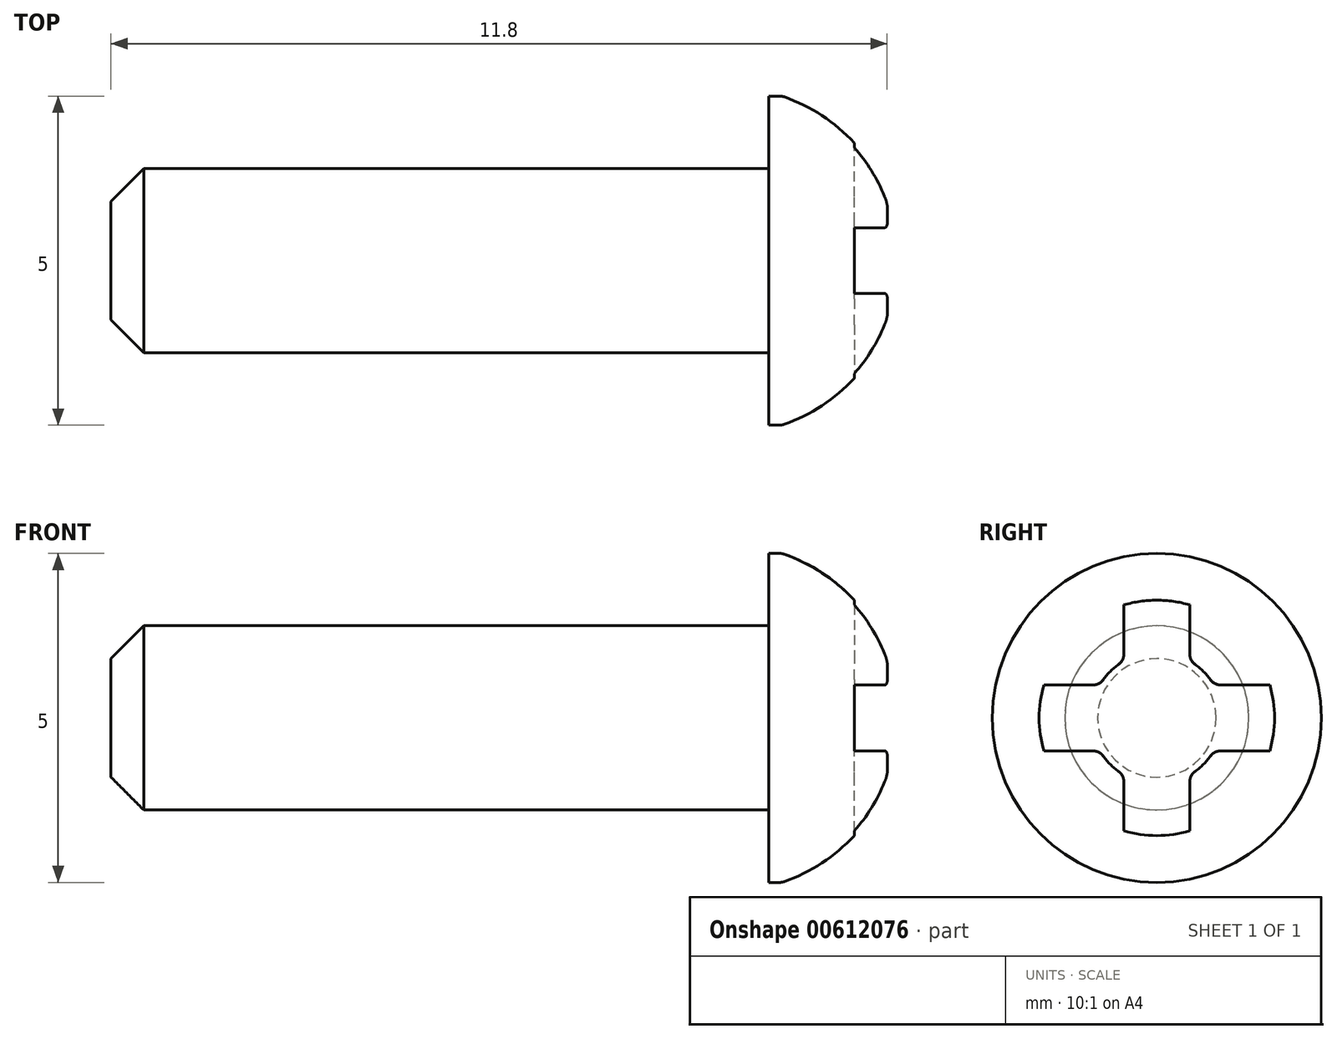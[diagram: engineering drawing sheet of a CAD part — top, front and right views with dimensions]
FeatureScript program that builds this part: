
annotation { "Feature Type Name" : "Feature", "Feature Type Description" : "" }
export const myFeature = defineFeature(function(context is Context, id is Id, definition is map)
    precondition{}
    {
        {
            var Q0;
            Q0=qCreatedBy(makeId("Front.planeOp"),FACE);
            var sketch = newSketch(context, id + "F0", { "sketchPlane" : qUnion([Q0])});
            skLineSegment(sketch, "E0", {"start": v(0, 1.4) * mm, "end": v(0, 2.5) * mm});
            skLineSegment(sketch, "E1", {"start": v(0, 1.4) * mm, "end": v(-10, 1.4) * mm});
            skLineSegment(sketch, "E2", {"start": v(-10, 1.4) * mm, "end": v(-10, 0) * mm});
            skLineSegment(sketch, "E3", {"start": v(-10, 0) * mm, "end": v(2, 0) * mm});
            skLineSegment(sketch, "E4", {"start": v(0, 0) * mm, "end": v(32.43, 0) * mm, "construction": true});
            skLineSegment(sketch, "E5", {"start": v(0, 2.5) * mm, "end": v(0.2, 2.5) * mm});
            skArc(sketch, "E6", {"start": v(2, 0) * mm, "mid": v(1.5, 1.54) * mm, "end": v(0.2, 2.5) * mm});
            skLineSegment(sketch, "E7", {"start": v(2, 0) * mm, "end": v(2, 6.78) * mm, "construction": true});
            skSolve(sketch);
        }
        {
            var Q0;
            Q0=makeQuery(id+"F0.imprint","IMPRINT",FACE,{"disambiguationData":[TD([[makeQuery(id+"F0.imprint","IMPRINT",EDGE,{"derivedFrom":sQuery(id+"F0.wireOp",EDGE,"E0")}),-1.0]])]});
            var Q1;
            Q1=sQuery(id+"F0.wireOp",EDGE,"E4");
            revolve(context, id + "F1", {"entities" : qUnion([Q0]), "axis" : qUnion([Q1]), "revolveType" : RevolveType.FULL});
        }
        {
            var Q0;
            Q0=makeQuery(id+"F1.opRevolve","SWEPT_EDGE",EDGE,{"disambiguationData":[OSD([sQuery(id+"F0.wireOp",EDGE,"E1"),sQuery(id+"F0.wireOp",EDGE,"E2")])]});
            chamfer(context, id + "F2", {"entities" : qUnion([Q0]), "width" : .5 * mm, "tangentPropagation" : true});
        }
        {
            var Q0;
            Q0=qCreatedBy(makeId("Right.planeOp"),FACE);
            cPlane(context, id + "F3", {"entities" : qUnion([Q0]), "cplaneType" : CPlaneType.OFFSET, "offset" : 3 * mm, "width" : 150 * mm, "height" : 150 * mm});
        }
        {
            var Q0;
            Q0=qCreatedBy(id+"F3.planeOp",FACE);
            var sketch = newSketch(context, id + "F4", { "sketchPlane" : qUnion([Q0])});
            skLineSegment(sketch, "E8.bottom", {"start": v(0, 0) * mm, "end": v(3, 0) * mm, "construction": true});
            skLineSegment(sketch, "E8.top", {"start": v(0, 3) * mm, "end": v(0.5, 3) * mm});
            skLineSegment(sketch, "E8.left", {"start": v(0, 0) * mm, "end": v(0, 3) * mm, "construction": true});
            skLineSegment(sketch, "E8.right", {"start": v(3, 0) * mm, "end": v(3, 0.5) * mm});
            skLineSegment(sketch, "E9", {"start": v(0.5, 3) * mm, "end": v(0.5, 0.87) * mm});
            skLineSegment(sketch, "E10", {"start": v(0.87, 0.5) * mm, "end": v(3, 0.5) * mm});
            skArc(sketch, "E11", {"start": v(0.87, 0.5) * mm, "mid": v(0.7, 0.7) * mm, "end": v(0.5, 0.87) * mm});
            skLineSegment(sketch, "E12.0.MirrorCS", {"start": v(0, -3) * mm, "end": v(0.5, -3) * mm});
            skLineSegment(sketch, "E13.0.MirrorCS", {"start": v(0.5, -3) * mm, "end": v(0.5, -0.87) * mm});
            skArc(sketch, "E14.0.MirrorCS", {"start": v(0.87, -0.5) * mm, "mid": v(0.7, -0.7) * mm, "end": v(0.5, -0.87) * mm});
            skLineSegment(sketch, "E15.0.MirrorCS", {"start": v(0.87, -0.5) * mm, "end": v(3, -0.5) * mm});
            skLineSegment(sketch, "E16.0.MirrorCS", {"start": v(3, 0) * mm, "end": v(3, -0.5) * mm});
            skLineSegment(sketch, "E17.0.MirrorCS", {"start": v(0, 3) * mm, "end": v(-0.5, 3) * mm});
            skLineSegment(sketch, "E18.0.MirrorCS", {"start": v(-0.5, 3) * mm, "end": v(-0.5, 0.87) * mm});
            skArc(sketch, "E19.0.MirrorCS", {"start": v(-0.87, 0.5) * mm, "mid": v(-0.7, 0.7) * mm, "end": v(-0.5, 0.87) * mm});
            skLineSegment(sketch, "E20.0.MirrorCS", {"start": v(-0.87, 0.5) * mm, "end": v(-3, 0.5) * mm});
            skLineSegment(sketch, "E21.0.MirrorCS", {"start": v(-3, 0) * mm, "end": v(-3, 0.5) * mm});
            skLineSegment(sketch, "E22.0.MirrorCS", {"start": v(-3, 0) * mm, "end": v(-3, -0.5) * mm});
            skLineSegment(sketch, "E23.0.MirrorCS", {"start": v(-0.87, -0.5) * mm, "end": v(-3, -0.5) * mm});
            skArc(sketch, "E24.0.MirrorCS", {"start": v(-0.87, -0.5) * mm, "mid": v(-0.7, -0.7) * mm, "end": v(-0.5, -0.87) * mm});
            skLineSegment(sketch, "E25.0.MirrorCS", {"start": v(-0.5, -3) * mm, "end": v(-0.5, -0.87) * mm});
            skLineSegment(sketch, "E26.0.MirrorCS", {"start": v(0, -3) * mm, "end": v(-0.5, -3) * mm});
            skSolve(sketch);
        }
        {
            var Q0;
            Q0=makeQuery(id+"F4.imprint","IMPRINT",FACE,{"disambiguationData":[TD([[makeQuery(id+"F4.imprint","IMPRINT",EDGE,{"derivedFrom":sQuery(id+"F4.wireOp",EDGE,"E8.top")}),-1.0]])]});
            extrude(context, id + "F5", {"entities" : qUnion([Q0]), "operationType" : NewBodyOperationType.REMOVE, "oppositeDirection" : true, "depth" : 1.7 * mm, "offsetDistance" : 25 * mm});
        }
        {
            var Q0;
            Q0=makeQuery(id+"F5.boolean.opBoolean","COPY",EDGE,{"derivedFrom":makeQuery(id+"F5.opExtrude","SWEPT_EDGE",EDGE,{"disambiguationData":[OSD([sQuery(id+"F4.wireOp",EDGE,"E9"),sQuery(id+"F4.wireOp",EDGE,"E11")])]})});
            var Q1;
            Q1=makeQuery(id+"F5.boolean.opBoolean","COPY",EDGE,{"derivedFrom":makeQuery(id+"F5.opExtrude","SWEPT_EDGE",EDGE,{"disambiguationData":[OSD([sQuery(id+"F4.wireOp",EDGE,"E10"),sQuery(id+"F4.wireOp",EDGE,"E11")])]})});
            var Q2;
            Q2=makeQuery(id+"F5.boolean.opBoolean","COPY",EDGE,{"derivedFrom":makeQuery(id+"F5.opExtrude","SWEPT_EDGE",EDGE,{"disambiguationData":[OSD([sQuery(id+"F4.wireOp",EDGE,"E14.0.MirrorCS"),sQuery(id+"F4.wireOp",EDGE,"E15.0.MirrorCS")])]})});
            var Q3;
            Q3=makeQuery(id+"F5.boolean.opBoolean","COPY",EDGE,{"derivedFrom":makeQuery(id+"F5.opExtrude","SWEPT_EDGE",EDGE,{"disambiguationData":[OSD([sQuery(id+"F4.wireOp",EDGE,"E13.0.MirrorCS"),sQuery(id+"F4.wireOp",EDGE,"E14.0.MirrorCS")])]})});
            var Q4;
            Q4=makeQuery(id+"F5.boolean.opBoolean","COPY",EDGE,{"derivedFrom":makeQuery(id+"F5.opExtrude","SWEPT_EDGE",EDGE,{"disambiguationData":[OSD([sQuery(id+"F4.wireOp",EDGE,"E19.0.MirrorCS"),sQuery(id+"F4.wireOp",EDGE,"E20.0.MirrorCS")])]})});
            var Q5;
            Q5=makeQuery(id+"F5.boolean.opBoolean","COPY",EDGE,{"derivedFrom":makeQuery(id+"F5.opExtrude","SWEPT_EDGE",EDGE,{"disambiguationData":[OSD([sQuery(id+"F4.wireOp",EDGE,"E18.0.MirrorCS"),sQuery(id+"F4.wireOp",EDGE,"E19.0.MirrorCS")])]})});
            var Q6;
            Q6=makeQuery(id+"F5.boolean.opBoolean","COPY",EDGE,{"derivedFrom":makeQuery(id+"F5.opExtrude","SWEPT_EDGE",EDGE,{"disambiguationData":[OSD([sQuery(id+"F4.wireOp",EDGE,"E24.0.MirrorCS"),sQuery(id+"F4.wireOp",EDGE,"E25.0.MirrorCS")])]})});
            var Q7;
            Q7=makeQuery(id+"F5.boolean.opBoolean","COPY",EDGE,{"derivedFrom":makeQuery(id+"F5.opExtrude","SWEPT_EDGE",EDGE,{"disambiguationData":[OSD([sQuery(id+"F4.wireOp",EDGE,"E23.0.MirrorCS"),sQuery(id+"F4.wireOp",EDGE,"E24.0.MirrorCS")])]})});
            fillet(context, id + "F6", {"entities" : qUnion([Q0, Q1, Q2, Q3, Q4, Q5, Q6, Q7]), "radius" : .2 * mm, "tangentPropagation" : true, "allowEdgeOverflow" : false});
        }
        {
            var Q0;
            Q0=makeQuery(id+"F1.opRevolve","SWEPT_EDGE",EDGE,{"disambiguationData":[OSD([sQuery(id+"F0.wireOp",EDGE,"E5"),sQuery(id+"F0.wireOp",EDGE,"E6")])]});
            fillet(context, id + "F7", {"entities" : qUnion([Q0]), "radius" : .2 * mm, "tangentPropagation" : true, "allowEdgeOverflow" : false});
        }
    });
